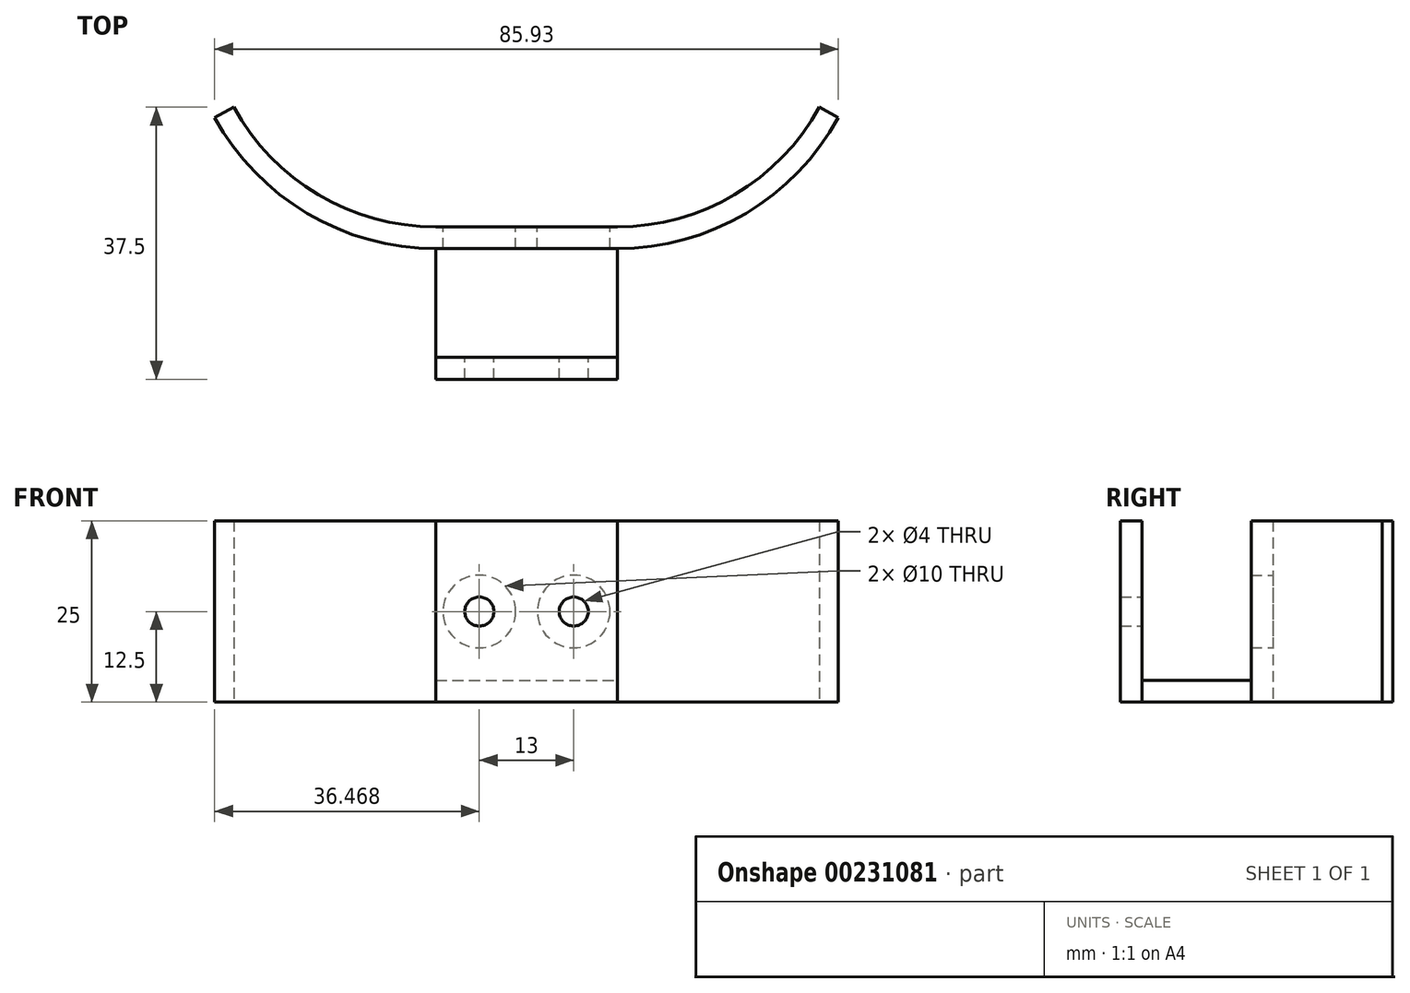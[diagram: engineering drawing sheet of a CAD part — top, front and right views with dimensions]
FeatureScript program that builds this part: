
annotation { "Feature Type Name" : "Feature", "Feature Type Description" : "" }
export const myFeature = defineFeature(function(context is Context, id is Id, definition is map)
    precondition{}
    {
        {
            var Q0;
            Q0=qCreatedBy(makeId("Top.planeOp"),FACE);
            var sketch = newSketch(context, id + "F0", { "sketchPlane" : qUnion([Q0])});
            skLineSegment(sketch, "E0.bottom", {"start": v(-21.5, 0) * mm, "end": v(3.5, 0) * mm});
            skLineSegment(sketch, "E0.top", {"start": v(-21.5, -3) * mm, "end": v(3.5, -3) * mm});
            skLineSegment(sketch, "E0.left", {"start": v(-21.5, 0) * mm, "end": v(-21.5, -3) * mm});
            skLineSegment(sketch, "E0.right", {"start": v(3.5, 0) * mm, "end": v(3.5, -3) * mm});
            skLineSegment(sketch, "E1.top", {"start": v(-21.5, 15) * mm, "end": v(3.5, 15) * mm});
            skLineSegment(sketch, "E1.left", {"start": v(-21.5, 0) * mm, "end": v(-21.5, 15) * mm});
            skLineSegment(sketch, "E1.right", {"start": v(3.5, 0) * mm, "end": v(3.5, 15) * mm});
            skArc(sketch, "E2", {"start": v(-21.5, 15) * mm, "mid": v(-39.2, 19.86) * mm, "end": v(-51.96, 33.06) * mm});
            skArc(sketch, "E3", {"start": v(3.5, 15) * mm, "mid": v(21.22, 19.86) * mm, "end": v(33.97, 33.06) * mm});
            skArc(sketch, "E4.0", {"start": v(-21.5, 18) * mm, "mid": v(-37.67, 22.44) * mm, "end": v(-49.32, 34.5) * mm});
            skLineSegment(sketch, "E4.1", {"start": v(-21.5, 18) * mm, "end": v(3.5, 18) * mm});
            skArc(sketch, "E4.2", {"start": v(3.5, 18) * mm, "mid": v(19.69, 22.44) * mm, "end": v(31.34, 34.5) * mm});
            skLineSegment(sketch, "E5", {"start": v(-51.96, 33.06) * mm, "end": v(-49.32, 34.5) * mm});
            skLineSegment(sketch, "E6", {"start": v(31.34, 34.5) * mm, "end": v(33.97, 33.06) * mm});
            skSolve(sketch);
        }
        {
            var Q0;
            Q0=makeQuery(id+"F0.imprint","IMPRINT",FACE,{"disambiguationData":[TD([[makeQuery(id+"F0.imprint","IMPRINT",EDGE,{"derivedFrom":sQuery(id+"F0.wireOp",EDGE,"E1.top")}),1.0]])]});
            var Q1;
            Q1=makeQuery(id+"F0.imprint","IMPRINT",FACE,{"disambiguationData":[TD([[makeQuery(id+"F0.imprint","IMPRINT",EDGE,{"derivedFrom":sQuery(id+"F0.wireOp",EDGE,"E0.top")}),1.0]])]});
            extrude(context, id + "F1", {"entities" : qUnion([Q0, Q1]), "depth" : 25 * mm});
        }
        {
            var Q0;
            Q0=makeQuery(id+"F0.imprint","IMPRINT",FACE,{"disambiguationData":[TD([[makeQuery(id+"F0.imprint","IMPRINT",EDGE,{"derivedFrom":sQuery(id+"F0.wireOp",EDGE,"E0.bottom")}),1.0]])]});
            extrude(context, id + "F2", {"entities" : qUnion([Q0]), "depth" : 3 * mm});
        }
        {
            var Q0;
            Q0=makeQuery(id+"F1.opExtrude","SWEPT_FACE",FACE,{"disambiguationData":[OSD([sQuery(id+"F0.wireOp",EDGE,"E4.1")])]});
            var sketch = newSketch(context, id + "F3", { "sketchPlane" : qUnion([Q0])});
            skCircle(sketch, "E7", {"center": v(15.5, 12.5) * mm, "radius": 2 * mm});
            skPoint(sketch, "E7.centerSnap0", {"position": v(21.5, 12.5) * mm});
            skCircle(sketch, "E8", {"center": v(2.5, 12.5) * mm, "radius": 2 * mm});
            skCircle(sketch, "E9", {"center": v(15.5, 12.5) * mm, "radius": 5 * mm});
            skCircle(sketch, "E10", {"center": v(2.5, 12.5) * mm, "radius": 5 * mm});
            skSolve(sketch);
        }
        {
            var Q0;
            Q0=makeQuery(id+"F3.imprint","IMPRINT",FACE,{"disambiguationData":[TD([[makeQuery(id+"F3.imprint","IMPRINT",EDGE,{"derivedFrom":sQuery(id+"F3.wireOp",EDGE,"E7")}),1.0]])]});
            var Q1;
            Q1=makeQuery(id+"F3.imprint","IMPRINT",FACE,{"disambiguationData":[TD([[makeQuery(id+"F3.imprint","IMPRINT",EDGE,{"derivedFrom":sQuery(id+"F3.wireOp",EDGE,"E8")}),1.0]])]});
            extrude(context, id + "F4", {"entities" : qUnion([Q0, Q1]), "operationType" : NewBodyOperationType.REMOVE, "oppositeDirection" : true, "depth" : 25 * mm});
        }
        {
            var Q0;
            Q0=makeQuery(id+"F3.imprint","IMPRINT",FACE,{"disambiguationData":[TD([[makeQuery(id+"F3.imprint","IMPRINT",EDGE,{"derivedFrom":sQuery(id+"F3.wireOp",EDGE,"E7")}),-1.0]])]});
            var Q1;
            Q1=makeQuery(id+"F3.imprint","IMPRINT",FACE,{"disambiguationData":[TD([[makeQuery(id+"F3.imprint","IMPRINT",EDGE,{"derivedFrom":sQuery(id+"F3.wireOp",EDGE,"E8")}),-1.0]])]});
            extrude(context, id + "F5", {"entities" : qUnion([Q0, Q1]), "operationType" : NewBodyOperationType.REMOVE, "oppositeDirection" : true, "depth" : 10 * mm});
        }
    });
